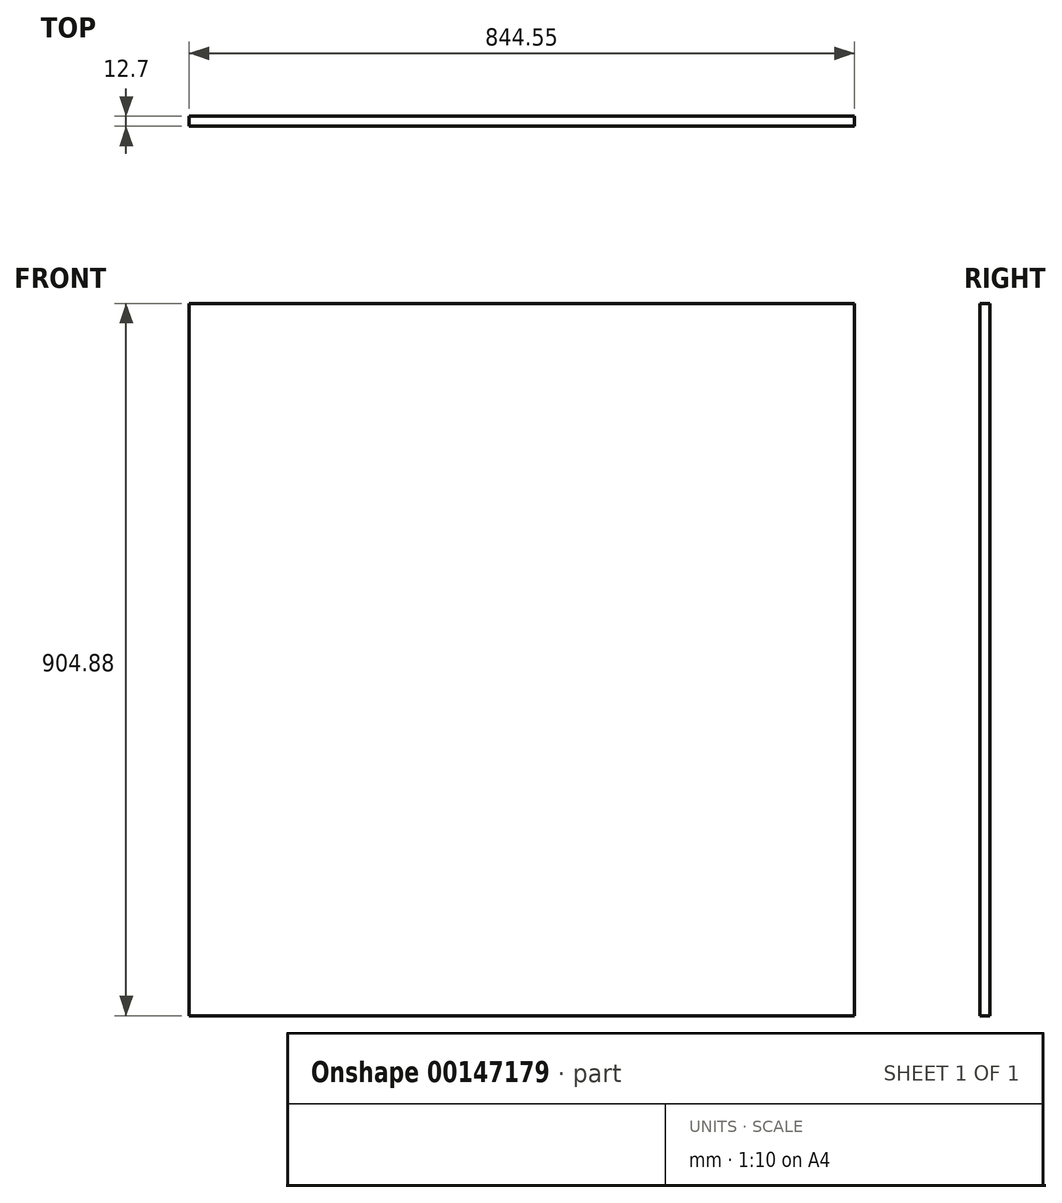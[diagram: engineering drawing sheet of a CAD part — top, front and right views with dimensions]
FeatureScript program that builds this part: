
annotation { "Feature Type Name" : "Feature", "Feature Type Description" : "" }
export const myFeature = defineFeature(function(context is Context, id is Id, definition is map)
    precondition{}
    {
        {
            var Q0;
            Q0=qCreatedBy(makeId("Front.planeOp"),FACE);
            var sketch = newSketch(context, id + "F0", { "sketchPlane" : qUnion([Q0])});
            skLineSegment(sketch, "E0.bottom", {"start": v(0, 0) * mm, "end": v(844.55, 0) * mm});
            skLineSegment(sketch, "E0.top", {"start": v(0, 904.88) * mm, "end": v(844.55, 904.88) * mm});
            skLineSegment(sketch, "E0.left", {"start": v(0, 0) * mm, "end": v(0, 904.88) * mm});
            skLineSegment(sketch, "E0.right", {"start": v(844.55, 0) * mm, "end": v(844.55, 904.88) * mm});
            skSolve(sketch);
        }
        {
            var Q0;
            Q0=makeQuery(id+"F0.imprint","IMPRINT",FACE,{"disambiguationData":[TD([[makeQuery(id+"F0.imprint","IMPRINT",EDGE,{"derivedFrom":sQuery(id+"F0.wireOp",EDGE,"E0.bottom")}),1.0]])]});
            extrude(context, id + "F1", {"entities" : qUnion([Q0]), "depth" : 12.7 * mm});
        }
    });
